# Revit family: Plumbing-Flushometer-Sloan-Valve-Dolphin-Type-I-Class-A_
name_source: partatom
category: Plumbing Fixtures
units: mm (PartAtom-declared; Revit-internal decimal feet)

## family parameters
Cut with Voids When Loaded = No
Host = Face
OmniClass Number = 23.45.05.14.99
OmniClass Title = Other Sanitary Washing Plumbing Fixtures
Part Type = Normal
Room Calculation Point = No
Round Connector Dimension = Use Diameter
Shared = No

## types (3) — shared parameters
Assembly Code = D2020300
CW Connection = Yes
Centerline of Supply from Top of Fixture = 24"
Centerline of Supply to Centerline of Valve = 4 3/4"
Default Elevation = 0"
Edition number = 1
Flush Rate = 1.6 gpf (6.0 Lpf)
HW Connection = No
Height = 28 7/8"
Keynote = 15410
Manufacturer = Sloan Valve
Operating Water Pressure = 15 – 80 PSI (103 – 552 kPa)
Product Material = Sloan Valve - Finish - Polished Chrome
Product data url = https://bimobject.com
URL = www.sloanvalve.com
Valve Pressure Drop = 0.00 psi
Vent Connection = No
Waste Connection = No
Water Inlet Connection Description = Water Inlet Connection
Water Inlet Connection Diameter = 1"
zero-valued in all types: CWFU, HWFU, WFU

## per-type parameters (varying)
| type | Description | Model | Part Number |
| DOLPHIN TYPE I CLASS A-1.6-A | 1.6 gpf, Polished Chrome Finish, Fixture Connection Top Spud, Single Flush, Right of Valve Inlet, Dolphin Exposed Manual Water Closet Flushometer. | DOLPHIN TYPE I CLASS A-1.6-A | 3057005 |
| DOLPHIN TYPE I CLASS A - DO9AAG CP Body ASM H5 3 1/4" TL CID#022 | Polished Chrome Finish, Fixture Connection Top Spud, Single Flush, Dolphin Exposed Manual Water Closet Flushometer. | DOLPHIN TYPE I CLASS A | 3950145 |
| DOLPHIN TYPE I CLASS A | Polished Chrome Finish, Fixture Connection Top Spud, Single Flush, Dolphin Exposed Manual Water Closet Flushometer. | DOLPHIN TYPE I CLASS A | 3950146 |

## geometry (parser evidence)
native form markers: Sweep x3
no freeform markers — native parametric forms only
